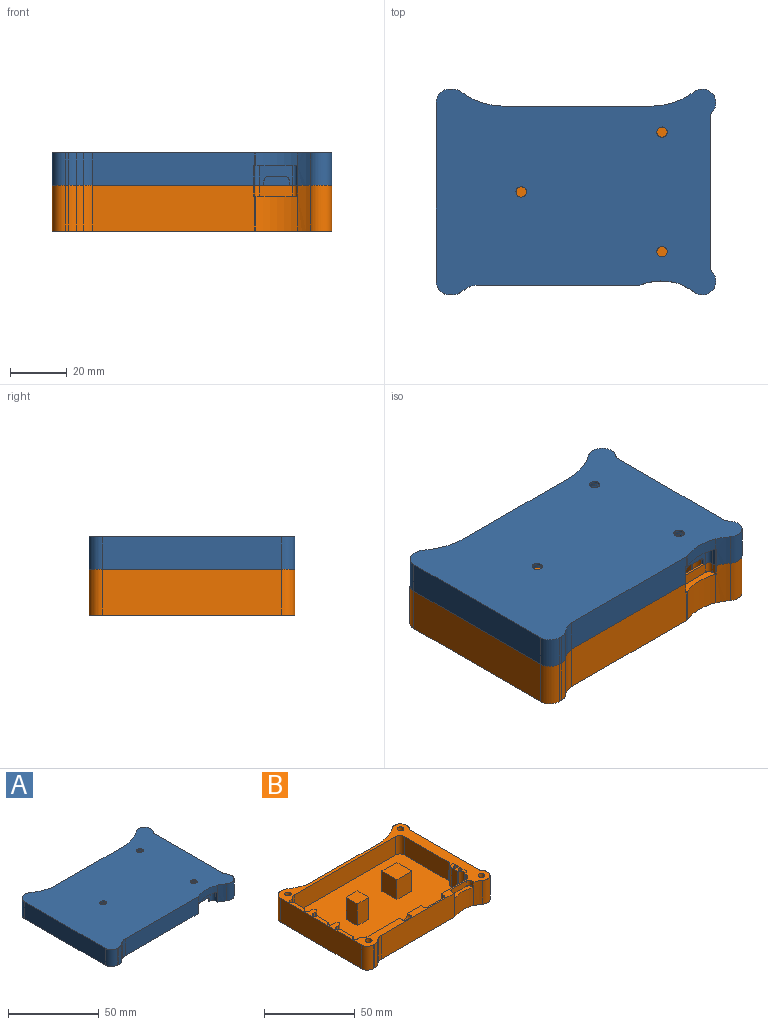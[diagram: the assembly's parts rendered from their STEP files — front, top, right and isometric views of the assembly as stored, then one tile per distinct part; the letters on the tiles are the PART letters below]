
ASSEMBLY  parts=2 mates=1
PART A: 118 faces, bbox 99.2x73.2x13.5 mm
  f0: plane 99.18x73.22mm, normal (0,0,-1), area 1099.4mm2, adj f1,f2,f3,f4,f5,f6,f7,f10
  f1: plane 2.67x1.58mm, normal (0,-1,0), area 4.2mm2, adj f0,f27,f98,f102
  f2: cylinder r=1.59mm len=8.05mm, axis (0,0,1), area 20.1mm2, adj f0,f41,f44,f48
  f3: plane 3.23x1.57mm, normal (0,1,0), area 5.1mm2, adj f0,f25,f101,f103
  f4: plane 9.56x3.23mm, normal (1,0,0), area 30.8mm2, adj f0,f25,f104,f105
  f5: plane 8.16x2.67mm, normal (1,0,0), area 21.8mm2, adj f0,f27,f106,f107
  f6: plane 8.16x2.67mm, normal (1,0,0), area 21.8mm2, adj f0,f46,f108,f109
  f7: cylinder r=4.76mm len=11.43mm, axis (0,0,-1), area 35mm2, adj f0,f8,f32,f68
  f8: plane 98.35x72.39mm, normal (0,0,1), area 6224.1mm2, adj f7,f9,f10,f11,f12,f28,f29,f32
  f9: cylinder r=1.27mm len=4.45mm, axis (0,0,1), area 2.1mm2, adj f8,f10,f11,f82
  f10: plane 57.01x11.43mm, normal (0,-1,0), area 649.5mm2, adj f0,f8,f9,f69,f79,f82
  f11: cylinder r=20.53mm len=14.57mm, axis (0,0,1), area 66.2mm2, adj f8,f9,f12,f82
  f12: cylinder r=25.4mm len=11.43mm, axis (0,0,-1), area 59.2mm2, adj f0,f8,f11,f36,f78,f82
  f13: cylinder r=1.6mm len=1.6mm, axis (0,-1,0), area 2.4mm2, adj f14,f15,f41,f75
  f14: plane 1.58x0.96mm, normal (1,0,0), area 1.5mm2, adj f0,f13,f41,f75
  f15: plane 5.69x0.96mm, normal (0,0,-1), area 5.5mm2, adj f13,f41,f42,f75
  f16: plane 11.74x2.84mm, normal (1,0,0), area 33.4mm2, adj f19,f21,f24,f48
  f17: plane 11.49x2.84mm, normal (0,-1,0), area 32.7mm2, adj f18,f19,f21,f48
  f18: cylinder r=0.25mm len=2.85mm, axis (0,0,1), area 1.1mm2, adj f17,f19,f20,f48
  f19: plane 12.25x12mm, normal (0,0,-1), area 146.9mm2, adj f16,f17,f18,f20,f21,f22,f23,f24
  f20: plane 11.74x2.84mm, normal (-1,0,0), area 33.4mm2, adj f18,f19,f22,f48
  f21: cylinder r=0.25mm len=2.85mm, axis (0,0,1), area 1.1mm2, adj f16,f17,f19,f48
  f22: cylinder r=0.25mm len=2.85mm, axis (0,0,1), area 1.1mm2, adj f19,f20,f23,f48
  f23: plane 11.49x2.84mm, normal (0,1,0), area 32.7mm2, adj f19,f22,f24,f48
  f24: cylinder r=0.25mm len=2.85mm, axis (0,0,1), area 1.1mm2, adj f16,f19,f23,f48
  f25: plane 16.89x3.42mm, normal (0,0,-1), area 37.9mm2, adj f3,f4,f26,f44,f100,f101,f103,f104
  f26: plane 3.23x1.57mm, normal (0,-1,0), area 5.1mm2, adj f0,f25,f100,f113
  f27: plane 15.48x3.42mm, normal (0,0,-1), area 35.4mm2, adj f1,f5,f40,f44,f63,f98,f99,f102
  f28: cylinder r=1.83mm len=3.66mm, axis (0,0,1), area 9mm2, adj f8,f31
  f29: cylinder r=1.83mm len=3.66mm, axis (0,0,1), area 9mm2, adj f8,f30
  f30: cone r=1.83mm half-angle=41deg, axis (0,0,-1), area 63.9mm2, adj f29,f48
  f31: cone r=1.77mm half-angle=41deg, axis (0,0,-1), area 63.9mm2, adj f28,f48
  f32: cylinder r=25.4mm len=15.24mm, axis (0,0,-1), area 186.8mm2, adj f0,f7,f8,f33
  f33: plane 51.56x11.43mm, normal (0,1,0), area 589.4mm2, adj f0,f8,f32,f34
  f34: cylinder r=25.4mm len=15.24mm, axis (0,0,-1), area 186.8mm2, adj f0,f8,f33,f35
  f35: cylinder r=4.76mm len=11.43mm, axis (0,0,-1), area 159.1mm2, adj f0,f8,f34,f71
  f36: cylinder r=4.76mm len=11.43mm, axis (0,0,-1), area 159.1mm2, adj f0,f8,f12,f70
  f37: cylinder r=25.4mm len=11.43mm, axis (0,0,-1), area 31.3mm2, adj f0,f8,f38,f69
  f38: cylinder r=4.76mm len=11.43mm, axis (0,0,-1), area 35mm2, adj f0,f8,f37,f67
  f39: plane 82.55x8.05mm, normal (0,-1,0), area 664.7mm2, adj f0,f40,f48,f87
  f40: cylinder r=1.59mm len=8.05mm, axis (0,0,1), area 19.9mm2, adj f0,f27,f39,f44,f48,f102
  f41: plane 82.55x8.05mm, normal (0,1,0), area 589.5mm2, adj f0,f2,f13,f14,f15,f42,f43,f48
  f42: cylinder r=1.6mm len=1.6mm, axis (0,-1,0), area 2.4mm2, adj f15,f41,f43,f75
  f43: plane 1.58x0.96mm, normal (-1,0,0), area 1.5mm2, adj f0,f41,f42,f75
  f44: plane 53.34x8.05mm, normal (1,0,0), area 292.6mm2, adj f0,f2,f25,f27,f40,f46,f48,f103
  f45: plane 2.67x1.57mm, normal (0,1,0), area 4.2mm2, adj f0,f46,f97,f112
  f46: plane 15.49x3.42mm, normal (0,0,-1), area 35.4mm2, adj f6,f44,f45,f47,f96,f97,f108,f109
  f47: plane 2.67x1.57mm, normal (0,-1,0), area 4.2mm2, adj f0,f46,f96,f110
  f48: plane 88.61x56.52mm, normal (0,0,-1), area 4590mm2, adj f2,f16,f17,f18,f20,f21,f22,f23
  f49: cylinder r=3.17mm len=6.35mm, axis (0,1,0), area 24.1mm2, adj f0,f41,f86
  f50: plane 2.74x2.19mm, normal (-0.62,0,-0.78), area 6.7mm2, adj f0,f41,f85,f116
  f51: plane 8.41x1.91mm, normal (0,0,-1), area 16mm2, adj f41,f84,f114,f116
  f52: plane 2.74x2.19mm, normal (0.62,0,-0.78), area 6.7mm2, adj f0,f41,f83,f114
  f53: cylinder r=1.83mm len=3.66mm, axis (0,0,1), area 9mm2, adj f8,f54
  f54: cone r=1.83mm half-angle=41deg, axis (0,0,-1), area 63.9mm2, adj f48,f53
  f55: cylinder r=1.52mm len=9.88mm, axis (0,0,1), area 94.6mm2, adj f0,f61
  f56: cylinder r=1.52mm len=9.88mm, axis (0,0,1), area 94.6mm2, adj f0,f62
  f57: cylinder r=1.52mm len=9.88mm, axis (0,0,1), area 94.6mm2, adj f0,f59
  f58: cylinder r=1.52mm len=9.88mm, axis (0,0,1), area 94.6mm2, adj f0,f60
  f59: cone r=0.8mm half-angle=59deg, axis (0,0,-1), area 8.5mm2, adj f57
  f60: cone r=0.8mm half-angle=59deg, axis (0,0,-1), area 8.5mm2, adj f58
  f61: cone r=0.8mm half-angle=59deg, axis (0,0,-1), area 8.5mm2, adj f55
  f62: cone r=0.8mm half-angle=59deg, axis (0,0,-1), area 8.5mm2, adj f56
  f63: plane 2.67x1.57mm, normal (0,1,0), area 4.2mm2, adj f0,f27,f99,f111
  f64: cylinder r=4.76mm len=11.43mm, axis (0,0,1), area 85.5mm2, adj f0,f8,f65,f67
  f65: plane 62.87x11.43mm, normal (-1,0,0), area 718.5mm2, adj f0,f8,f64,f66
  f66: cylinder r=4.76mm len=11.43mm, axis (0,0,1), area 85.5mm2, adj f0,f8,f65,f68
  f67: plane 11.43x1.07mm, normal (0,-1,0), area 12.2mm2, adj f0,f8,f38,f64
  f68: plane 11.43x1.07mm, normal (0,1,0), area 12.2mm2, adj f0,f7,f8,f66
  f69: cylinder r=6.35mm len=11.43mm, axis (0,0,1), area 38.9mm2, adj f0,f8,f10,f37
  f70: cylinder r=3.43mm len=11.43mm, axis (0,0,1), area 27.7mm2, adj f0,f8,f36,f72
  f71: cylinder r=3.43mm len=11.43mm, axis (0,0,1), area 27.7mm2, adj f0,f8,f35,f72
  f72: plane 52.21x11.43mm, normal (1,0,0), area 596.8mm2, adj f0,f8,f70,f71
  f73: plane 3.18x1.59mm, normal (0,1,0), area 4mm2, adj f0,f86
  f74: plane 10.79x0.95mm, normal (0,1,0), area 9.1mm2, adj f0,f83,f84,f85
  f75: plane 11.84x6.99mm, normal (0,-1,0), area 55.6mm2, adj f0,f13,f14,f15,f42,f43,f76,f81
  f76: cylinder r=1.59mm len=6.99mm, axis (0,0,-1), area 17.4mm2, adj f0,f75,f77,f82
  f77: plane 6.99x1.55mm, normal (-1,0,0), area 10.8mm2, adj f0,f76,f78,f82
  f78: cylinder r=0.25mm len=6.99mm, axis (0,0,-1), area 2mm2, adj f0,f12,f77,f82
  f79: cylinder r=0.25mm len=6.99mm, axis (0,0,-1), area 2.8mm2, adj f0,f10,f80,f82
  f80: plane 6.99x1.77mm, normal (1,0,0), area 12.3mm2, adj f0,f79,f81,f82
  f81: cylinder r=1.59mm len=6.99mm, axis (0,0,-1), area 17.4mm2, adj f0,f75,f80,f82
  f82: plane 15.41x3.61mm, normal (0,0,-1), area 37.4mm2, adj f9,f10,f11,f12,f75,f76,f77,f78
  f83: cylinder r=1.59mm len=3.73mm, axis (0.78,0,0.62), area 6.3mm2, adj f0,f52,f74,f115
  f84: cylinder r=1.59mm len=8.41mm, axis (1,0,0), area 21mm2, adj f51,f74,f115,f117
  f85: cylinder r=1.59mm len=3.73mm, axis (0.78,0,-0.62), area 6.3mm2, adj f0,f50,f74,f117
  f86: torus R=1.59mm, axis (0,1,0), area 20.4mm2, adj f0,f49,f73
  f87: cylinder r=1.59mm len=8.05mm, axis (0,0,-1), area 20.1mm2, adj f0,f39,f48,f88
  f88: plane 16.02x8.05mm, normal (-1,0,0), area 129mm2, adj f0,f48,f87,f89
  f89: cylinder r=1.27mm len=8.05mm, axis (0,0,-1), area 12mm2, adj f0,f48,f88,f90
  f90: cylinder r=3.43mm len=8.05mm, axis (0,0,-1), area 32.5mm2, adj f0,f48,f89,f91
  f91: plane 12.63x8.05mm, normal (-1,0,0), area 101.7mm2, adj f0,f48,f90,f92
  f92: cylinder r=3.43mm len=8.05mm, axis (0,0,-1), area 32.5mm2, adj f0,f48,f91,f93
  f93: cylinder r=1.27mm len=8.05mm, axis (0,0,-1), area 12mm2, adj f0,f48,f92,f94
  f94: plane 16.02x8.05mm, normal (-1,0,0), area 129mm2, adj f0,f48,f93,f95
  f95: cylinder r=1.59mm len=8.05mm, axis (0,0,-1), area 20.1mm2, adj f0,f41,f48,f94
  f96: cylinder r=1.59mm len=3.16mm, axis (0,0,-1), area 12.7mm2, adj f0,f46,f47,f108
  f97: cylinder r=1.59mm len=3.16mm, axis (0,0,-1), area 12.7mm2, adj f0,f45,f46,f109
  f98: cylinder r=1.59mm len=3.16mm, axis (0,0,-1), area 12.7mm2, adj f0,f1,f27,f106
  f99: cylinder r=1.59mm len=3.16mm, axis (0,0,-1), area 12.7mm2, adj f0,f27,f63,f107
  f100: cylinder r=1.59mm len=3.23mm, axis (0,0,-1), area 15.4mm2, adj f0,f25,f26,f104
  f101: cylinder r=1.59mm len=3.23mm, axis (0,0,-1), area 15.4mm2, adj f0,f3,f25,f105
  f102: cylinder r=0.25mm len=2.67mm, axis (0,0,1), area 1mm2, adj f0,f1,f27,f40
  f103: cylinder r=0.25mm len=3.23mm, axis (0,0,-1), area 1.3mm2, adj f0,f3,f25,f44
  f104: cylinder r=0.25mm len=3.23mm, axis (0,0,-1), area 1.2mm2, adj f0,f4,f25,f100
  f105: cylinder r=0.25mm len=3.23mm, axis (0,0,-1), area 1.2mm2, adj f0,f4,f25,f101
  f106: cylinder r=0.25mm len=2.67mm, axis (0,0,-1), area 1mm2, adj f0,f5,f27,f98
  f107: cylinder r=0.25mm len=2.67mm, axis (0,0,-1), area 1mm2, adj f0,f5,f27,f99
  f108: cylinder r=0.25mm len=2.67mm, axis (0,0,-1), area 1mm2, adj f0,f6,f46,f96
  f109: cylinder r=0.25mm len=2.67mm, axis (0,0,-1), area 1mm2, adj f0,f6,f46,f97
  f110: cylinder r=0.25mm len=2.67mm, axis (0,0,-1), area 1.1mm2, adj f0,f44,f46,f47
  f111: cylinder r=0.25mm len=2.67mm, axis (0,0,-1), area 1.1mm2, adj f0,f27,f44,f63
  f112: cylinder r=0.25mm len=2.67mm, axis (0,0,-1), area 1.1mm2, adj f0,f44,f45,f46
  f113: cylinder r=0.25mm len=3.23mm, axis (0,0,-1), area 1.3mm2, adj f0,f25,f26,f44
  f114: cylinder r=1.59mm len=1.91mm, axis (0,-1,0), area 2mm2, adj f41,f51,f52,f115
  f115: sphere r=1.59mm, area 2.3mm2, adj f83,f84,f114
  f116: cylinder r=1.59mm len=1.91mm, axis (0,-1,0), area 2mm2, adj f41,f50,f51,f117
  f117: sphere r=1.59mm, area 1.7mm2, adj f84,f85,f116
PART B: 146 faces, bbox 98.3x72.4x18.3 mm
  f0: plane 85.66x56.52mm, normal (0,0,1), area 4408mm2, adj f1,f2,f3,f21,f22,f24,f25,f29
  f1: plane 13.12x1.52mm, normal (1,0,0), area 20mm2, adj f0,f34,f91,f130
  f2: cylinder r=3.17mm len=3.19mm, axis (0,0,1), area 3.8mm2, adj f0,f65,f89,f134
  f3: cylinder r=3.17mm len=3.19mm, axis (0,0,1), area 3.8mm2, adj f0,f53,f54,f132
  f4: plane 10.92x9.56mm, normal (1,0,0), area 104.4mm2, adj f18,f34,f135,f136
  f5: plane 13.21x8.16mm, normal (1,0,0), area 107.8mm2, adj f18,f53,f137,f138
  f6: plane 13.21x8.16mm, normal (1,0,0), area 107.8mm2, adj f18,f65,f139,f140
  f7: plane 16.08x1.07mm, normal (0,1,0), area 17.2mm2, adj f10,f18,f19,f46
  f8: plane 62.87x16.08mm, normal (-1,0,0), area 1010.8mm2, adj f10,f11,f18,f19
  f9: plane 16.08x1.07mm, normal (0,-1,0), area 17.2mm2, adj f11,f17,f18,f19
  f10: cylinder r=4.76mm len=16.08mm, axis (0,0,-1), area 120.3mm2, adj f7,f8,f18,f19
  f11: cylinder r=4.76mm len=16.08mm, axis (0,0,-1), area 120.3mm2, adj f8,f9,f18,f19
  f12: cylinder r=6.35mm len=16.08mm, axis (0,0,1), area 54.7mm2, adj f13,f16,f18,f19
  f13: plane 57.01x16.08mm, normal (0,-1,0), area 915.5mm2, adj f12,f15,f18,f19,f30,f107
  f14: cylinder r=20.53mm len=14.57mm, axis (0,0,-1), area 182.7mm2, adj f15,f19,f30,f76
  f15: cylinder r=1.27mm len=12.27mm, axis (0,0,-1), area 5.8mm2, adj f13,f14,f19,f30
  f16: cylinder r=25.4mm len=16.08mm, axis (0,0,-1), area 44.1mm2, adj f12,f17,f18,f19
  f17: cylinder r=4.76mm len=16.08mm, axis (0,0,-1), area 49.3mm2, adj f9,f16,f18,f19
  f18: plane 98.35x72.39mm, normal (0,0,1), area 1181mm2, adj f4,f5,f6,f7,f8,f9,f10,f11
  f19: plane 98.35x72.39mm, normal (0,0,-1), area 6038mm2, adj f7,f8,f9,f10,f11,f12,f13,f14
  f20: plane 1.18x0.94mm, normal (0,-1,0), area 1.1mm2, adj f18,f62,f81,f85
  f21: cylinder r=0.25mm len=13.39mm, axis (0,0,-1), area 5.3mm2, adj f0,f40,f51,f87
  f22: cylinder r=0.25mm len=13.39mm, axis (0,0,1), area 3.5mm2, adj f0,f49,f62,f73
  f23: plane 3.94x1.65mm, normal (1,0,0), area 6.5mm2, adj f18,f42,f50,f121
  f24: plane 12.45x1.44mm, normal (-0.7,0.71,0), area 25.2mm2, adj f0,f18,f71,f94
  f25: plane 78.74x12.45mm, normal (0,-1,0), area 980mm2, adj f0,f18,f70,f123
  f26: cylinder r=1.1mm len=17.02mm, axis (0,0,-1), area 118.1mm2, adj f19,f62
  f27: cylinder r=1.83mm len=13.48mm, axis (0,0,1), area 154.9mm2, adj f18,f38
  f28: cone r=1.83mm half-angle=41deg, axis (0,0,-1), area 63.9mm2, adj f19,f90
  f29: plane 13.21x2.86mm, normal (0,1,0), area 24.2mm2, adj f0,f18,f65,f109,f117,f142
  f30: plane 15.41x3.61mm, normal (0,0,1), area 37.4mm2, adj f13,f14,f15,f37,f44,f69,f76,f78
  f31: cylinder r=0.25mm len=14.66mm, axis (0,0,-1), area 5.8mm2, adj f0,f41,f68,f97
  f32: cylinder r=3.43mm len=12.45mm, axis (0,0,1), area 67mm2, adj f0,f18,f57,f88
  f33: cylinder r=1.1mm len=17.02mm, axis (0,0,-1), area 118.1mm2, adj f19,f62
  f34: plane 17.48x5.35mm, normal (0,0,1), area 38.8mm2, adj f1,f4,f55,f75,f91,f113,f114,f126
  f35: plane 13.21x2.86mm, normal (0,-1,0), area 24.2mm2, adj f0,f18,f53,f112,f119,f143
  f36: cylinder r=0.23mm len=12.45mm, axis (0,0,1), area 2.9mm2, adj f0,f18,f48,f70
  f37: cylinder r=1.59mm len=3.81mm, axis (0,0,-1), area 9.5mm2, adj f18,f30,f44,f69
  f38: cone r=1.83mm half-angle=41deg, axis (0,0,-1), area 63.9mm2, adj f19,f27
  f39: cylinder r=4.76mm len=16.08mm, axis (0,0,-1), area 223.8mm2, adj f18,f19,f84,f102
  f40: plane 13.39x11.18mm, normal (0,-1,0), area 149.6mm2, adj f0,f21,f79,f87
  f41: plane 8.89x8.89mm, normal (0,0,1), area 79mm2, adj f31,f43,f47,f66,f68,f93,f97,f98
  f42: cylinder r=0.25mm len=3.94mm, axis (0,0,-1), area 1.6mm2, adj f18,f23,f50,f88
  f43: cylinder r=0.25mm len=14.66mm, axis (0,0,-1), area 5.8mm2, adj f0,f41,f66,f98
  f44: plane 11.84x3.81mm, normal (0,-1,0), area 45.1mm2, adj f18,f30,f37,f104
  f45: cylinder r=4.76mm len=16.08mm, axis (0,0,-1), area 223.8mm2, adj f18,f19,f76,f101
  f46: cylinder r=4.76mm len=16.08mm, axis (0,0,-1), area 49.3mm2, adj f7,f18,f19,f77
  f47: cylinder r=0.25mm len=14.66mm, axis (0,0,-1), area 5.8mm2, adj f0,f41,f68,f98
  f48: plane 13.21x2.13mm, normal (0,-1,0), area 28.1mm2, adj f18,f36,f65,f110,f116
  f49: plane 13.39x4.89mm, normal (-1,0,0), area 65.4mm2, adj f0,f22,f62,f71
  f50: plane 16.38x3.49mm, normal (0,0,1), area 54.4mm2, adj f23,f42,f52,f86,f88,f105,f120,f121
  f51: plane 13.39x11.18mm, normal (1,0,0), area 149.6mm2, adj f0,f21,f64,f87
  f52: plane 3.94x1.65mm, normal (-1,0,0), area 6.5mm2, adj f18,f50,f86,f120
  f53: plane 14.99x9.21mm, normal (0,0,1), area 111.2mm2, adj f3,f5,f35,f54,f63,f74,f111,f112
  f54: plane 6.86x0.76mm, normal (-1,0,0), area 5.2mm2, adj f0,f3,f53,f74
  f55: plane 10.92x1.84mm, normal (0,1,0), area 20.1mm2, adj f18,f34,f113,f145
  f56: plane 2.12x0.94mm, normal (0,1,0), area 2mm2, adj f18,f62,f82,f96
  f57: plane 12.45x1.22mm, normal (-1,0,0), area 15.2mm2, adj f0,f18,f32,f73
  f58: cylinder r=1.83mm len=13.48mm, axis (0,0,1), area 154.9mm2, adj f18,f67
  f59: plane 51.56x16.08mm, normal (0,1,0), area 829mm2, adj f18,f19,f77,f84
  f60: plane 13.39x11.18mm, normal (0,1,0), area 149.6mm2, adj f0,f61,f64,f87
  f61: cylinder r=0.25mm len=13.39mm, axis (0,0,-1), area 5.3mm2, adj f0,f60,f87,f99
  f62: plane 10.48x3.48mm, normal (0,0,1), area 24.2mm2, adj f20,f22,f26,f33,f49,f56,f71,f73
  f63: plane 13.21x2.86mm, normal (0,1,0), area 24.2mm2, adj f0,f18,f53,f111,f118,f144
  f64: cylinder r=0.25mm len=13.39mm, axis (0,0,-1), area 5.3mm2, adj f0,f51,f60,f87
  f65: plane 14.99x9.21mm, normal (0,0,1), area 111.2mm2, adj f2,f6,f29,f48,f83,f89,f109,f110
  f66: plane 14.66x8.38mm, normal (1,0,0), area 122.8mm2, adj f0,f41,f43,f93
  f67: cone r=1.83mm half-angle=41deg, axis (0,0,-1), area 64.1mm2, adj f19,f58
  f68: plane 14.66x8.38mm, normal (-1,0,0), area 122.8mm2, adj f0,f31,f41,f47
  f69: plane 3.81x1.55mm, normal (-1,0,0), area 5.9mm2, adj f18,f30,f37,f78
  f70: cylinder r=3.43mm len=12.45mm, axis (0,0,1), area 43.8mm2, adj f0,f18,f25,f36
  f71: cylinder r=3.43mm len=13.39mm, axis (0,0,1), area 36.2mm2, adj f0,f18,f24,f49,f62,f82
  f72: cylinder r=1.83mm len=13.48mm, axis (0,0,1), area 154.9mm2, adj f18,f92
  f73: cylinder r=3.43mm len=13.39mm, axis (0,0,1), area 47.2mm2, adj f0,f18,f22,f57,f62,f81
  f74: cylinder r=3.17mm len=3.19mm, axis (0,0,1), area 3.8mm2, adj f0,f53,f54,f131
  f75: plane 10.92x1.77mm, normal (0,-1,0), area 19.3mm2, adj f18,f34,f114,f141
  f76: cylinder r=25.4mm len=16.08mm, axis (0,0,-1), area 83.8mm2, adj f14,f18,f19,f30,f45,f78
  f77: cylinder r=25.4mm len=16.08mm, axis (0,0,-1), area 262.8mm2, adj f18,f19,f46,f59
  f78: cylinder r=0.25mm len=3.81mm, axis (0,0,1), area 1.1mm2, adj f18,f30,f69,f76
  f79: cylinder r=0.25mm len=13.39mm, axis (0,0,-1), area 5.3mm2, adj f0,f40,f87,f99
  f80: plane 34.08x12.45mm, normal (-1,0,0), area 424.2mm2, adj f0,f18,f94,f123
  f81: cylinder r=0.25mm len=0.94mm, axis (0,0,1), area 0.4mm2, adj f18,f20,f62,f73
  f82: cylinder r=0.25mm len=0.94mm, axis (0,0,1), area 0.2mm2, adj f18,f56,f62,f71
  f83: cylinder r=3.17mm len=3.19mm, axis (0,0,1), area 3.8mm2, adj f0,f65,f89,f133
  f84: cylinder r=25.4mm len=16.08mm, axis (0,0,-1), area 262.8mm2, adj f18,f19,f39,f59
  f85: cylinder r=0.25mm len=0.94mm, axis (0,0,1), area 0.4mm2, adj f18,f20,f62,f95
  f86: cylinder r=0.25mm len=3.94mm, axis (0,0,1), area 1.6mm2, adj f18,f50,f52,f88
  f87: plane 11.68x11.68mm, normal (0,0,1), area 136.5mm2, adj f21,f40,f51,f60,f61,f64,f79,f99
  f88: plane 77.06x12.45mm, normal (0,1,0), area 878.7mm2, adj f0,f18,f32,f42,f50,f86,f91,f100
  f89: plane 6.86x0.76mm, normal (-1,0,0), area 5.2mm2, adj f0,f2,f65,f83
  f90: cylinder r=1.83mm len=13.48mm, axis (0,0,1), area 154.9mm2, adj f18,f28
  f91: cylinder r=3.43mm len=12.45mm, axis (0,0,-1), area 52.8mm2, adj f0,f1,f18,f34,f88,f145
  f92: cone r=1.83mm half-angle=41deg, axis (0,0,-1), area 63.9mm2, adj f19,f72
  f93: cylinder r=0.25mm len=14.66mm, axis (0,0,-1), area 5.8mm2, adj f0,f41,f66,f97
  f94: cylinder r=3.43mm len=12.45mm, axis (0,0,1), area 33.8mm2, adj f0,f18,f24,f80
  f95: plane 9.97x0.94mm, normal (1,0,0), area 9.4mm2, adj f18,f62,f85,f96
  f96: cylinder r=0.25mm len=0.94mm, axis (0,0,1), area 0.4mm2, adj f18,f56,f62,f95
  f97: plane 14.66x8.38mm, normal (0,-1,0), area 122.8mm2, adj f0,f31,f41,f93
  f98: plane 14.66x8.38mm, normal (0,1,0), area 122.8mm2, adj f0,f41,f43,f47
  f99: plane 13.39x11.18mm, normal (-1,0,0), area 149.6mm2, adj f0,f61,f79,f87
  f100: cylinder r=3.17mm len=6.35mm, axis (0,1,0), area 24.1mm2, adj f18,f88,f122
  f101: cylinder r=3.43mm len=16.08mm, axis (0,0,1), area 39mm2, adj f18,f19,f45,f103
  f102: cylinder r=3.43mm len=16.08mm, axis (0,0,1), area 39mm2, adj f18,f19,f39,f103
  f103: plane 52.21x16.08mm, normal (1,0,0), area 839.5mm2, adj f18,f19,f101,f102
  f104: cylinder r=1.59mm len=3.81mm, axis (0,0,1), area 9.5mm2, adj f18,f30,f44,f108
  f105: plane 12.7x3.94mm, normal (0,1,0), area 50mm2, adj f18,f50,f120,f121
  f106: plane 3.18x1.59mm, normal (0,1,0), area 4mm2, adj f18,f122
  f107: cylinder r=0.25mm len=3.81mm, axis (0,0,1), area 1.5mm2, adj f13,f18,f30,f108
  f108: plane 3.81x1.77mm, normal (1,0,0), area 6.7mm2, adj f18,f30,f104,f107
  f109: cylinder r=1.59mm len=13.21mm, axis (0,0,1), area 63mm2, adj f18,f29,f65,f139
  f110: cylinder r=1.59mm len=13.21mm, axis (0,0,1), area 63mm2, adj f18,f48,f65,f140
  f111: cylinder r=1.59mm len=13.21mm, axis (0,0,1), area 63mm2, adj f18,f53,f63,f137
  f112: cylinder r=1.59mm len=13.21mm, axis (0,0,1), area 63mm2, adj f18,f35,f53,f138
  f113: cylinder r=1.59mm len=10.92mm, axis (0,0,1), area 52.1mm2, adj f18,f34,f55,f135
  f114: cylinder r=1.59mm len=10.92mm, axis (0,0,1), area 52.1mm2, adj f18,f34,f75,f136
  f115: cylinder r=1.59mm len=1.35mm, axis (0,0,1), area 1.2mm2, adj f0,f65,f116,f134
  f116: plane 0.76x0.74mm, normal (0,-1,0), area 0.6mm2, adj f0,f48,f65,f115
  f117: cylinder r=1.59mm len=1.36mm, axis (0,0,1), area 1.2mm2, adj f0,f29,f65,f133
  f118: cylinder r=1.59mm len=1.36mm, axis (0,0,1), area 1.2mm2, adj f0,f53,f63,f131
  f119: cylinder r=1.59mm len=1.36mm, axis (0,0,1), area 1.2mm2, adj f0,f35,f53,f132
  f120: cylinder r=1.59mm len=3.94mm, axis (0,0,1), area 9.8mm2, adj f18,f50,f52,f105
  f121: cylinder r=1.59mm len=3.94mm, axis (0,0,1), area 9.8mm2, adj f18,f23,f50,f105
  f122: torus R=1.59mm, axis (0,1,0), area 20.4mm2, adj f18,f100,f106
  f123: cylinder r=3.43mm len=12.45mm, axis (0,0,1), area 67mm2, adj f0,f18,f25,f80
  f124: plane 12.45x1.91mm, normal (0.43,-0.9,0), area 26.4mm2, adj f0,f18,f129,f143
  f125: plane 12.45x1.91mm, normal (0.43,0.9,0), area 26.4mm2, adj f0,f18,f129,f142
  f126: plane 12.45x1.94mm, normal (0.43,-0.9,0), area 23.6mm2, adj f0,f18,f34,f128,f130,f141
  f127: plane 12.45x1.94mm, normal (0.43,0.9,0), area 26.8mm2, adj f0,f18,f128,f144
  f128: cylinder r=0.64mm len=12.45mm, axis (0,0,1), area 17.7mm2, adj f0,f18,f126,f127
  f129: cylinder r=0.64mm len=12.45mm, axis (0,0,1), area 17.8mm2, adj f0,f18,f124,f125
  f130: cylinder r=3.43mm len=3.09mm, axis (0,0,-1), area 5.9mm2, adj f0,f1,f34,f126
  f131: cylinder r=0.25mm len=0.76mm, axis (0,0,1), area 0.2mm2, adj f0,f53,f74,f118
  f132: cylinder r=0.25mm len=0.76mm, axis (0,0,1), area 0.2mm2, adj f0,f3,f53,f119
  f133: cylinder r=0.25mm len=0.76mm, axis (0,0,1), area 0.2mm2, adj f0,f65,f83,f117
  f134: cylinder r=0.25mm len=0.76mm, axis (0,0,1), area 0.2mm2, adj f0,f2,f65,f115
  f135: cylinder r=0.25mm len=10.92mm, axis (0,0,1), area 4mm2, adj f4,f18,f34,f113
  f136: cylinder r=0.25mm len=10.92mm, axis (0,0,1), area 4mm2, adj f4,f18,f34,f114
  f137: cylinder r=0.25mm len=13.21mm, axis (0,0,1), area 4.8mm2, adj f5,f18,f53,f111
  f138: cylinder r=0.25mm len=13.21mm, axis (0,0,1), area 4.8mm2, adj f5,f18,f53,f112
  f139: cylinder r=0.25mm len=13.21mm, axis (0,0,1), area 4.8mm2, adj f6,f18,f65,f109
  f140: cylinder r=0.25mm len=13.21mm, axis (0,0,1), area 4.8mm2, adj f6,f18,f65,f110
  f141: cylinder r=0.25mm len=10.92mm, axis (0,0,1), area 1.2mm2, adj f18,f34,f75,f126
  f142: cylinder r=0.25mm len=12.45mm, axis (0,0,1), area 1.4mm2, adj f0,f18,f29,f125
  f143: cylinder r=0.25mm len=12.45mm, axis (0,0,1), area 1.4mm2, adj f0,f18,f35,f124
  f144: cylinder r=0.25mm len=12.45mm, axis (0,0,1), area 1.4mm2, adj f0,f18,f63,f127
  f145: cylinder r=0.25mm len=10.92mm, axis (0,0,-1), area 3.3mm2, adj f18,f34,f55,f91
PLACE A t=(-49.11,32.78,22.17)mm
PLACE B at identity
MATE fastened A.f55 <-> B.f90  axis (0,0,-1) through (0,-62.87,16.46)mm
